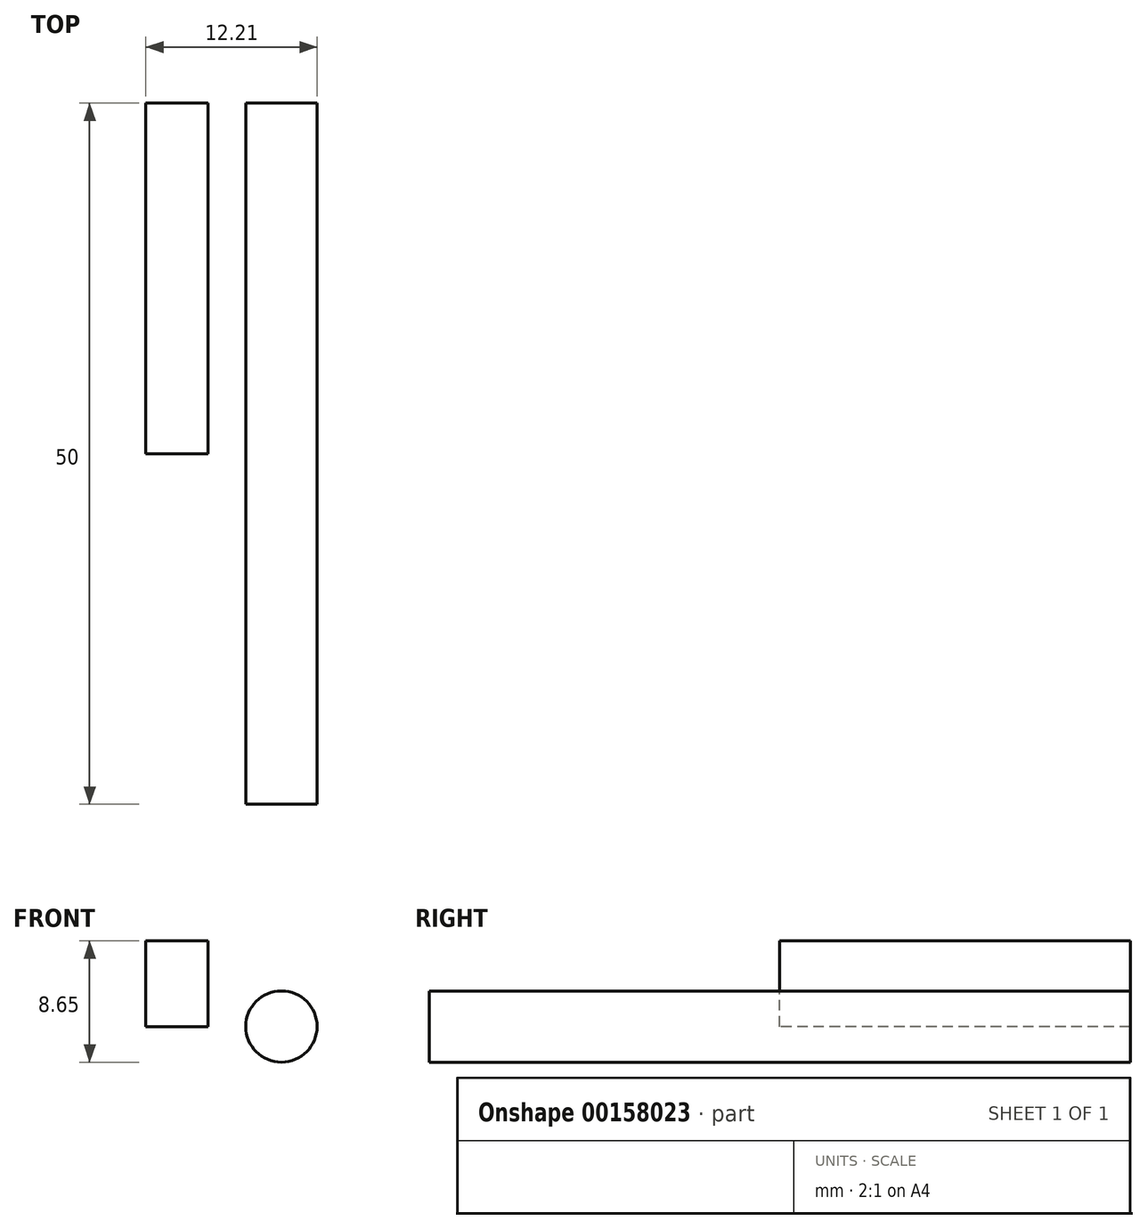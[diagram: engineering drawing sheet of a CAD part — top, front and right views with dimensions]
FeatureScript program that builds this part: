
annotation { "Feature Type Name" : "Feature", "Feature Type Description" : "" }
export const myFeature = defineFeature(function(context is Context, id is Id, definition is map)
    precondition{}
    {
        {
            var Q0;
            Q0=qCreatedBy(makeId("Front.planeOp"),FACE);
            var sketch = newSketch(context, id + "F0", { "sketchPlane" : qUnion([Q0])});
            skCircle(sketch, "E0", {"center": v(0, 0) * mm, "radius": 10 * mm});
            skSolve(sketch);
        }
        {
            var Q0;
            Q0 = qSketchRegion(id + "F0", true);
            extrude(context, id + "F1", {"entities" : qUnion([Q0]), "depth" : 25 * mm});
        }
        {
            var Q0;
            Q0=makeQuery(id+"F1.opExtrude","CAP_FACE",FACE,{"disambiguationData":[OSD([sQuery(id+"F0.wireOp",EDGE,"E0")])],"isStart":false});
            var sketch = newSketch(context, id + "F5", { "sketchPlane" : qUnion([Q0])});
            skCircle(sketch, "E1", {"center": v(5.24, 0) * mm, "radius": 2.54 * mm});
            skSolve(sketch);
        }
        {
            var Q0;
            Q0 = qSketchRegion(id + "F5", true);
            extrude(context, id + "F2", {"entities" : qUnion([Q0]), "operationType" : NewBodyOperationType.ADD, "depth" : 25 * mm});
        }
        {
            var Q0;
            Q0=makeQuery(id+"F1.opExtrude","CAP_FACE",FACE,{"disambiguationData":[OSD([sQuery(id+"F0.wireOp",EDGE,"E0")])],"isStart":false});
            var sketch = newSketch(context, id + "F3", { "sketchPlane" : qUnion([Q0])});
            skLineSegment(sketch, "E2.bottom", {"start": v(0, 0) * mm, "end": v(-4.43, 0) * mm});
            skLineSegment(sketch, "E2.top", {"start": v(0, 6.1) * mm, "end": v(-4.43, 6.1) * mm});
            skLineSegment(sketch, "E2.left", {"start": v(0, 0) * mm, "end": v(0, 6.1) * mm});
            skLineSegment(sketch, "E2.right", {"start": v(-4.43, 0) * mm, "end": v(-4.43, 6.1) * mm});
            skPoint(sketch, "E2.middle", {"position": v(-2.22, 3.05) * mm});
            skSolve(sketch);
        }
        {
            var Q0;
            Q0=makeQuery(id+"F3.imprint","IMPRINT",FACE,{"disambiguationData":[TD([[makeQuery(id+"F3.imprint","IMPRINT",EDGE,{"derivedFrom":sQuery(id+"F3.wireOp",EDGE,"E2.bottom")}),1.0]])]});
            extrude(context, id + "F4", {"entities" : qUnion([Q0]), "operationType" : NewBodyOperationType.REMOVE, "endBound" : BoundingType.THROUGH_ALL, "oppositeDirection" : true, "depth" : 25 * mm});
        }
    });
